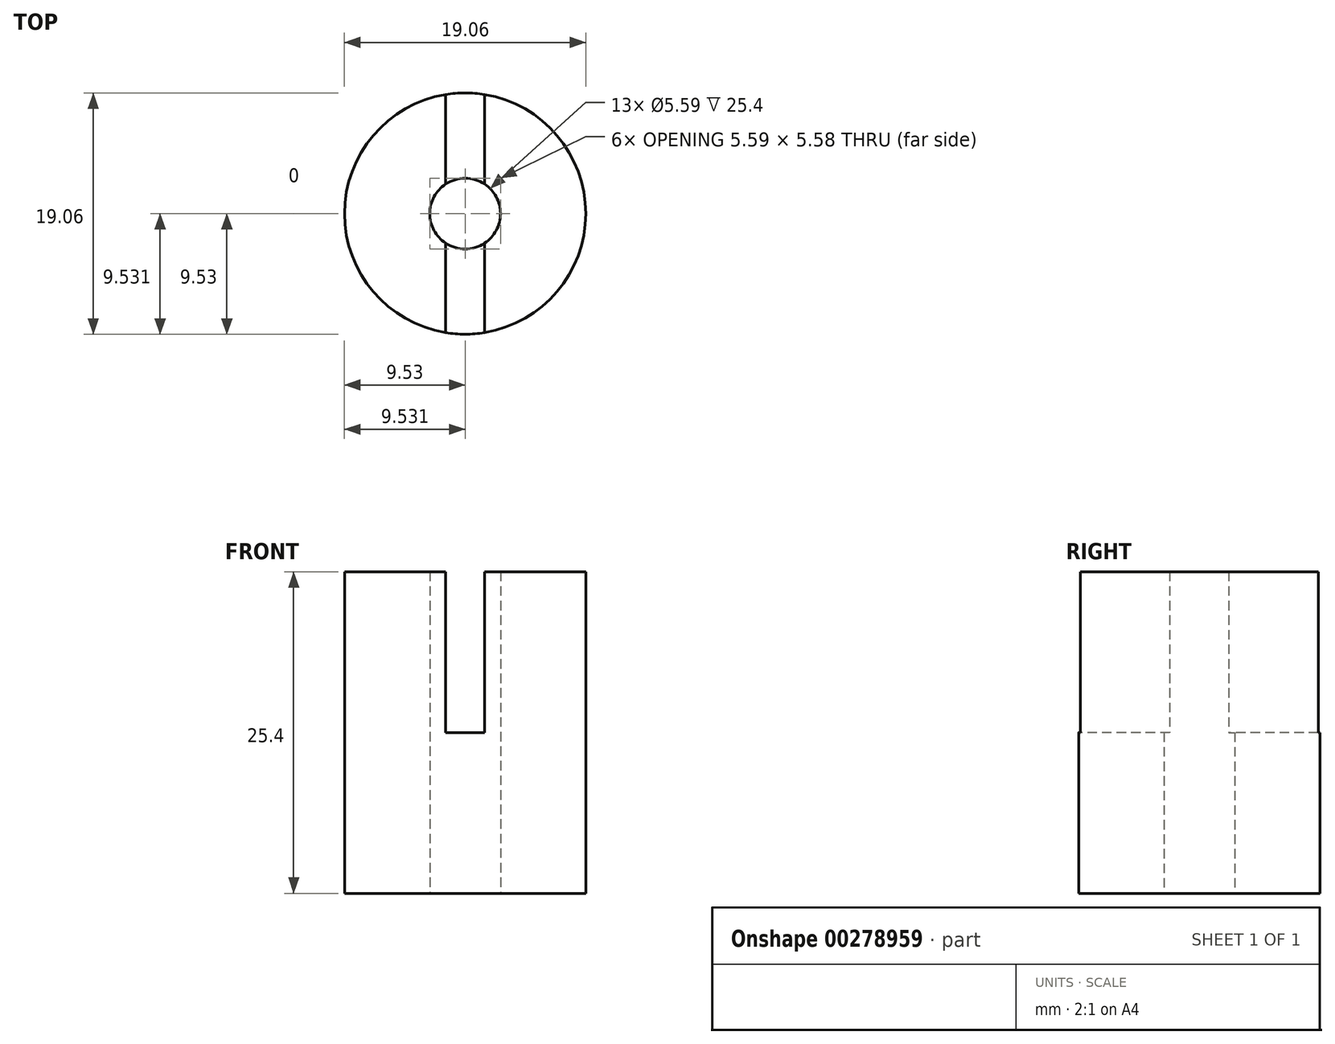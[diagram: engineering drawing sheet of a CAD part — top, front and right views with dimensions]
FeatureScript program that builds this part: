
annotation { "Feature Type Name" : "Feature", "Feature Type Description" : "" }
export const myFeature = defineFeature(function(context is Context, id is Id, definition is map)
    precondition{}
    {
        {
            var Q0;
            Q0=qCreatedBy(makeId("Top.planeOp"),FACE);
            var sketch = newSketch(context, id + "F0", { "sketchPlane" : qUnion([Q0])});
            skCircle(sketch, "E0", {"center": v(0, 0) * mm, "radius": 9.53 * mm});
            skCircle(sketch, "E1", {"center": v(0, 0) * mm, "radius": 2.8 * mm});
            skSolve(sketch);
        }
        {
            var Q0;
            Q0 = qSketchRegion(id + "F0", true);
            var Q1;
            Q1=makeQuery(id+"F0.imprint","IMPRINT",FACE,{"disambiguationData":[TD([[makeQuery(id+"F0.imprint","IMPRINT",EDGE,{"derivedFrom":sQuery(id+"F0.wireOp",EDGE,"E1")}),1.0]])]});
            extrude(context, id + "F1", {"entities" : qUnion([Q0, Q1]), "depth" : 25.4 * mm});
        }
        {
            var Q0;
            Q0=qCreatedBy(makeId("Front.planeOp"),FACE);
            var sketch = newSketch(context, id + "F2", { "sketchPlane" : qUnion([Q0])});
            skLineSegment(sketch, "E2.bottom", {"start": v(1.54, 38.1) * mm, "end": v(-1.54, 38.1) * mm});
            skLineSegment(sketch, "E2.top", {"start": v(1.54, 12.7) * mm, "end": v(-1.54, 12.7) * mm});
            skLineSegment(sketch, "E2.left", {"start": v(1.54, 38.1) * mm, "end": v(1.54, 12.7) * mm});
            skLineSegment(sketch, "E2.right", {"start": v(-1.54, 38.1) * mm, "end": v(-1.54, 12.7) * mm});
            skPoint(sketch, "E2.middle", {"position": v(0, 25.4) * mm});
            skSolve(sketch);
        }
        {
            var Q0;
            Q0=makeQuery(id+"F2.imprint","IMPRINT",FACE,{"disambiguationData":[TD([[makeQuery(id+"F2.imprint","IMPRINT",EDGE,{"derivedFrom":sQuery(id+"F2.wireOp",EDGE,"E2.bottom")}),1.0]])]});
            extrude(context, id + "F3", {"entities" : qUnion([Q0]), "operationType" : NewBodyOperationType.REMOVE, "endBound" : BoundingType.SYMMETRIC, "oppositeDirection" : true, "depth" : 25.4 * mm});
        }
        {
            var Q0;
            Q0=makeQuery(id+"F0.imprint","IMPRINT",FACE,{"disambiguationData":[TD([[makeQuery(id+"F0.imprint","IMPRINT",EDGE,{"derivedFrom":sQuery(id+"F0.wireOp",EDGE,"E1")}),1.0]])]});
            var Q1;
            {var subQ0=sQuery(id+"F0.wireOp",EDGE,"E0");Q1=makeQuery(id+"F3.boolean.opBoolean","SPLIT",FACE,{"disambiguationData":[TD([makeQuery(id+"F3.opExtrude","SWEPT_FACE",FACE,{"disambiguationData":[OSD([sQuery(id+"F2.wireOp",EDGE,"E2.right")])]})])],"derivedFrom":makeQuery(id+"F1.opExtrude","CAP_FACE",FACE,{"disambiguationData":[OSD([subQ0])],"isStart":false})});}
            extrude(context, id + "F4", {"entities" : qUnion([Q0]), "operationType" : NewBodyOperationType.REMOVE, "endBound" : BoundingType.UP_TO_SURFACE, "endBoundEntityFace" : qUnion([Q1]), "depth" : 11.43 * mm});
        }
    });
